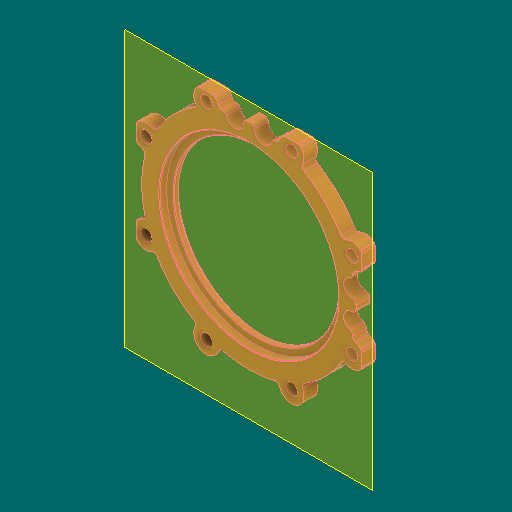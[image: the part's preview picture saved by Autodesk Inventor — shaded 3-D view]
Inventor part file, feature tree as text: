
AUTODESK INVENTOR PART (.ipt)
format: ipt  version: 2023.1 (Build 271208000, 208)  size: 336,896 bytes
history: native  units: in
note: dims shown in document units (in); Inventor stores cm internally (conversion verified against a paired STEP export)
features: other x3, sketch x2, plane x1
ambient origin geometry x8: Origin, YZ Plane, XZ Plane, XY Plane, X Axis, Y Axis, Z Axis, Center Point
bodies: Solid1 (feature_tree)
feature tree (6):
  other  "UpperRaceRing.ipt"
  other  "Solid1::UpperRaceRing.ipt"
  other  "TaggingFeature1"
  sketch  "Sketch1"  dims[d0=0.3937in]
  sketch  "Sketch2"
  plane  "Work Plane1"
